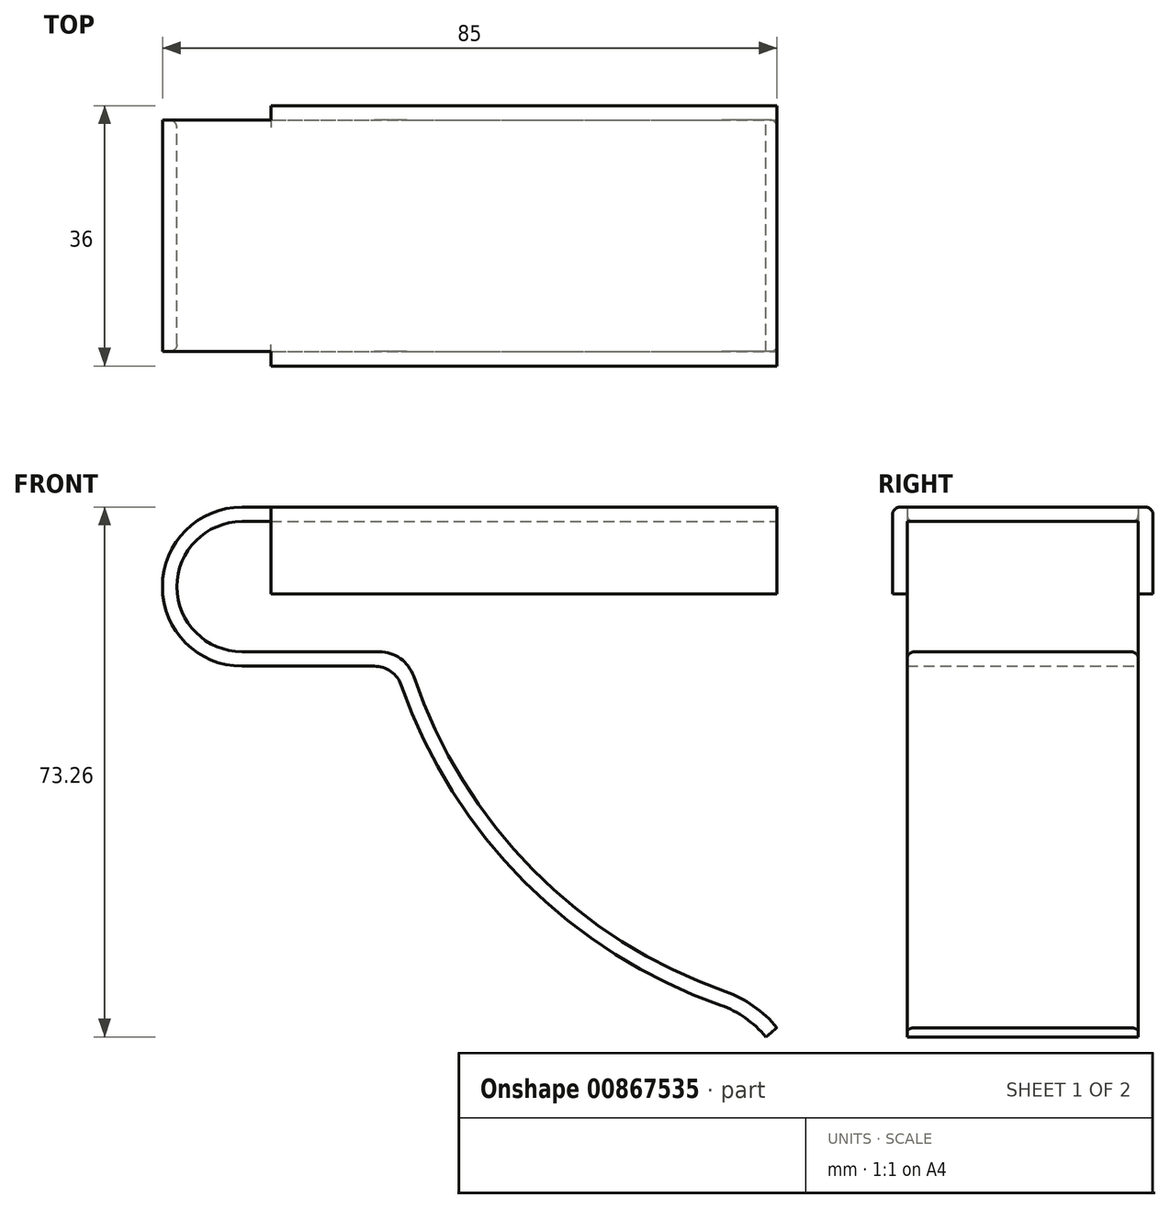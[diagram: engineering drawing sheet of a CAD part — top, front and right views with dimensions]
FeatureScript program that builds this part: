
annotation { "Feature Type Name" : "Feature", "Feature Type Description" : "" }
export const myFeature = defineFeature(function(context is Context, id is Id, definition is map)
    precondition{}
    {
        {
            var Q0;
            Q0=qCreatedBy(makeId("Front.planeOp"),FACE);
            var sketch = newSketch(context, id + "F0", { "sketchPlane" : qUnion([Q0])});
            skArc(sketch, "E0", {"start": v(0, 9) * mm, "mid": v(-9, 0) * mm, "end": v(0, -9) * mm});
            skLineSegment(sketch, "E1", {"start": v(0, 9) * mm, "end": v(74, 9) * mm});
            skLineSegment(sketch, "E2", {"start": v(0, -9) * mm, "end": v(19, -9) * mm});
            skArc(sketch, "E3", {"start": v(23.74, -12.4) * mm, "mid": v(40.28, -39.18) * mm, "end": v(66.88, -56) * mm});
            skArc(sketch, "E4", {"start": v(74, -61) * mm, "mid": v(70.79, -58) * mm, "end": v(66.88, -56) * mm});
            skPoint(sketch, "E5.visualSharp", {"position": v(22.68, -9) * mm});
            skArc(sketch, "E5.filletArc", {"start": v(23.74, -12.4) * mm, "mid": v(21.91, -9.94) * mm, "end": v(19, -9) * mm});
            skLineSegment(sketch, "E6.0", {"start": v(0, 11) * mm, "end": v(74, 11) * mm});
            skArc(sketch, "E6.1", {"start": v(72.45, -62.26) * mm, "mid": v(69.64, -59.64) * mm, "end": v(66.22, -57.89) * mm});
            skArc(sketch, "E6.2", {"start": v(22.06, -13.68) * mm, "mid": v(39.1, -40.82) * mm, "end": v(66.22, -57.89) * mm});
            skLineSegment(sketch, "E6.3", {"start": v(0, -11) * mm, "end": v(18.29, -11) * mm});
            skArc(sketch, "E6.4", {"start": v(0, 11) * mm, "mid": v(-11, 0) * mm, "end": v(0, -11) * mm});
            skLineSegment(sketch, "E7", {"start": v(74, 11) * mm, "end": v(74, 9) * mm});
            skLineSegment(sketch, "E8", {"start": v(74, -61) * mm, "end": v(72.45, -62.26) * mm});
            skPoint(sketch, "E9.visualSharp", {"position": v(21.18, -11) * mm});
            skArc(sketch, "E9.filletArc", {"start": v(22.06, -13.68) * mm, "mid": v(20.6, -11.74) * mm, "end": v(18.29, -11) * mm});
            skSolve(sketch);
        }
        {
            var Q0;
            Q0 = qSketchRegion(id + "F0", true);
            extrude(context, id + "F1", {"entities" : qUnion([Q0]), "depth" : 16 * mm, "offsetDistance" : 25 * mm});
        }
        {
            var Q0;
            Q0=makeQuery(id+"F1.opExtrude","CAP_FACE",FACE,{"disambiguationData":[OSD([sQuery(id+"F0.wireOp",EDGE,"E0"),sQuery(id+"F0.wireOp",EDGE,"E1"),sQuery(id+"F0.wireOp",EDGE,"E2"),sQuery(id+"F0.wireOp",EDGE,"E3"),sQuery(id+"F0.wireOp",EDGE,"E4"),sQuery(id+"F0.wireOp",EDGE,"E5.filletArc"),sQuery(id+"F0.wireOp",EDGE,"E6.0"),sQuery(id+"F0.wireOp",EDGE,"E6.1"),sQuery(id+"F0.wireOp",EDGE,"E6.2"),sQuery(id+"F0.wireOp",EDGE,"E6.3"),sQuery(id+"F0.wireOp",EDGE,"E6.4"),sQuery(id+"F0.wireOp",EDGE,"E7"),sQuery(id+"F0.wireOp",EDGE,"E8"),sQuery(id+"F0.wireOp",EDGE,"E9.filletArc")])],"isStart":false});
            var sketch = newSketch(context, id + "F2", { "sketchPlane" : qUnion([Q0])});
            skLineSegment(sketch, "E10.bottom", {"start": v(4, 11) * mm, "end": v(74, 11) * mm});
            skLineSegment(sketch, "E10.top", {"start": v(4, -1) * mm, "end": v(74, -1) * mm});
            skLineSegment(sketch, "E10.left", {"start": v(4, 11) * mm, "end": v(4, -1) * mm});
            skLineSegment(sketch, "E10.right", {"start": v(74, 11) * mm, "end": v(74, -1) * mm});
            skSolve(sketch);
        }
        {
            var Q0;
            {var subQ0=sQuery(id+"F2.wireOp",EDGE,"E10.bottom");Q0=makeQuery(id+"F2.imprint","IMPRINT",FACE,{"disambiguationData":[TD([[makeQuery(id+"F2.imprint","IMPRINT",EDGE,{"derivedFrom":subQ0}),-1.0]])]});}
            var Q1;
            {var subQ0=sQuery(id+"F2.wireOp",EDGE,"E10.top");Q1=makeQuery(id+"F2.imprint","IMPRINT",FACE,{"disambiguationData":[TD([[makeQuery(id+"F2.imprint","IMPRINT",EDGE,{"derivedFrom":subQ0}),1.0]])]});}
            extrude(context, id + "F3", {"entities" : qUnion([Q0, Q1]), "operationType" : NewBodyOperationType.ADD, "depth" : 2 * mm, "offsetDistance" : 25 * mm});
        }
        {
            var Q0;
            Q0=makeQuery(id+"F3.opExtrude","CAP_EDGE",EDGE,{"disambiguationData":[OSD([sQuery(id+"F2.wireOp",EDGE,"E10.bottom")])],"isStart":false});
            var Q1;
            {var subQ0=sQuery(id+"F0.wireOp",EDGE,"E1");Q1=makeQuery(id+"F3.boolean.opBoolean","SPLIT",EDGE,{"disambiguationData":[topologyDisambiguationEdgeConnected([makeQuery(id+"F3.opExtrude","CAP_FACE",FACE,{"disambiguationData":[OSD([sQuery(id+"F2.wireOp",EDGE,"E10.bottom"),sQuery(id+"F2.wireOp",EDGE,"E10.top"),sQuery(id+"F2.wireOp",EDGE,"E10.left"),sQuery(id+"F2.wireOp",EDGE,"E10.right")])],"isStart":true})])],"derivedFrom":makeQuery(id+"F1.opExtrude","CAP_EDGE",EDGE,{"disambiguationData":[OSD([subQ0])],"isStart":false})});}
            fillet(context, id + "F4", {"entities" : qUnion([Q0, Q1]), "radius" : 1 * mm, "tangentPropagation" : true, "allowEdgeOverflow" : false});
        }
        {
            var Q0;
            Q0=makeQuery(id+"F1.opExtrude","SWEPT_BODY",BODY,{"disambiguationData":[OSD([sQuery(id+"F0.wireOp",EDGE,"E0"),sQuery(id+"F0.wireOp",EDGE,"E1"),sQuery(id+"F0.wireOp",EDGE,"E2"),sQuery(id+"F0.wireOp",EDGE,"E3"),sQuery(id+"F0.wireOp",EDGE,"E4"),sQuery(id+"F0.wireOp",EDGE,"E5.filletArc"),sQuery(id+"F0.wireOp",EDGE,"E6.0"),sQuery(id+"F0.wireOp",EDGE,"E6.1"),sQuery(id+"F0.wireOp",EDGE,"E6.2"),sQuery(id+"F0.wireOp",EDGE,"E6.3"),sQuery(id+"F0.wireOp",EDGE,"E6.4"),sQuery(id+"F0.wireOp",EDGE,"E7"),sQuery(id+"F0.wireOp",EDGE,"E8"),sQuery(id+"F0.wireOp",EDGE,"E9.filletArc")])]});
            var Q1;
            Q1=qCreatedBy(makeId("Front.planeOp"),FACE);
            mirror(context, id + "F5", {"operationType" : NewBodyOperationType.ADD, "entities" : qUnion([Q0]), "mirrorPlane" : qUnion([Q1])});
        }
    });
